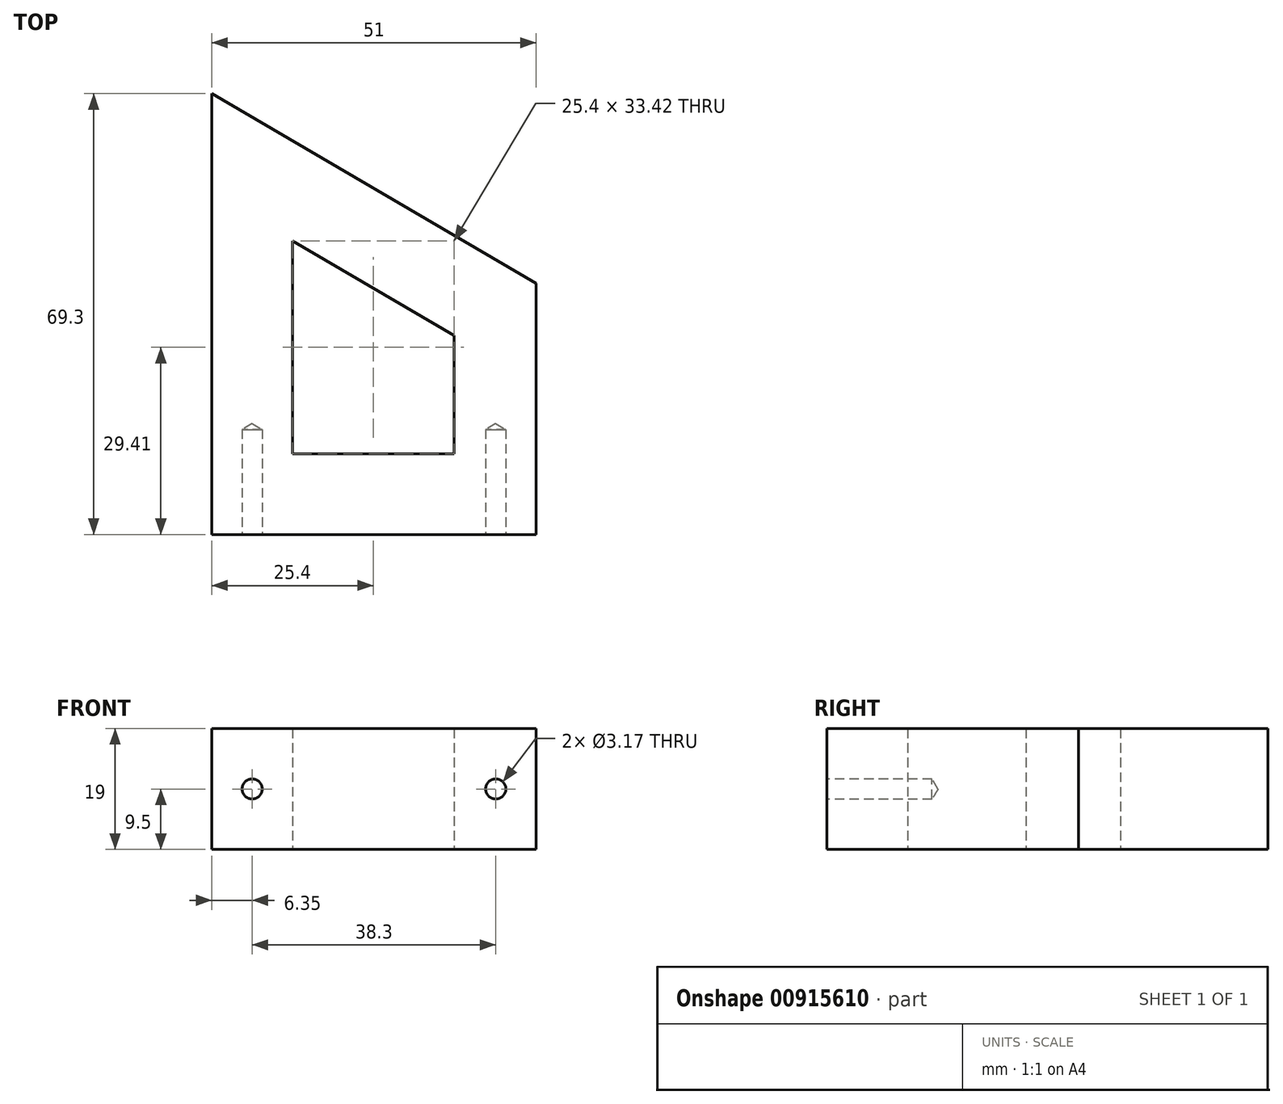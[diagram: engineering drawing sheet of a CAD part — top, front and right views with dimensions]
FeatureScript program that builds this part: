
annotation { "Feature Type Name" : "Feature", "Feature Type Description" : "" }
export const myFeature = defineFeature(function(context is Context, id is Id, definition is map)
    precondition{}
    {
        {
            var Q0;
            Q0=qCreatedBy(makeId("Top.planeOp"),FACE);
            var sketch = newSketch(context, id + "F0", { "sketchPlane" : qUnion([Q0])});
            skLineSegment(sketch, "E0", {"start": v(0, 0) * mm, "end": v(0, 69.3) * mm});
            skLineSegment(sketch, "E1", {"start": v(0, 0) * mm, "end": v(51, 0) * mm});
            skLineSegment(sketch, "E2", {"start": v(51, 0) * mm, "end": v(51, 39.5) * mm});
            skLineSegment(sketch, "E3", {"start": v(51, 39.5) * mm, "end": v(0, 69.3) * mm});
            skLineSegment(sketch, "E4", {"start": v(12.7, 12.7) * mm, "end": v(12.7, 46.12) * mm});
            skLineSegment(sketch, "E5", {"start": v(12.7, 46.12) * mm, "end": v(38.1, 31.28) * mm});
            skLineSegment(sketch, "E6", {"start": v(12.7, 12.7) * mm, "end": v(38.1, 12.7) * mm});
            skLineSegment(sketch, "E7", {"start": v(38.1, 12.7) * mm, "end": v(38.1, 31.28) * mm});
            skPoint(sketch, "E8.endSnap0", {"position": v(12.7, 29.41) * mm});
            skSolve(sketch);
        }
        {
            var Q0;
            Q0=makeQuery(id+"F0.imprint","IMPRINT",FACE,{"disambiguationData":[TD([[makeQuery(id+"F0.imprint","IMPRINT",EDGE,{"derivedFrom":sQuery(id+"F0.wireOp",EDGE,"E0")}),-1.0]])]});
            extrude(context, id + "F1", {"entities" : qUnion([Q0]), "depth" : 19 * mm, "offsetDistance" : 25.4 * mm});
        }
        {
            var Q0;
            Q0=makeQuery(id+"F1.opExtrude","SWEPT_FACE",FACE,{"disambiguationData":[OSD([sQuery(id+"F0.wireOp",EDGE,"E1")])]});
            var sketch = newSketch(context, id + "F2", { "sketchPlane" : qUnion([Q0])});
            skLineSegment(sketch, "E9", {"start": v(0, 9.5) * mm, "end": v(51, 9.5) * mm, "construction": true});
            skCircle(sketch, "E10", {"center": v(6.35, 9.5) * mm, "radius": 1.08 * mm});
            skCircle(sketch, "E11", {"center": v(44.65, 9.5) * mm, "radius": 1.08 * mm});
            skSolve(sketch);
        }
        {
            var Q0;
            Q0 = qSketchRegion(id + "F2", true);
            extrude(context, id + "F3", {"entities" : qUnion([Q0]), "operationType" : NewBodyOperationType.ADD, "oppositeDirection" : true, "depth" : 19.05 * mm, "hasOffset" : true, "offsetDistance" : 25.4 * mm});
        }
        {
            var Q0;
            Q0=makeQuery(id+"F1.opExtrude","SWEPT_FACE",FACE,{"disambiguationData":[OSD([sQuery(id+"F0.wireOp",EDGE,"E1")])]});
            var sketch = newSketch(context, id + "F4", { "sketchPlane" : qUnion([Q0])});
            skLineSegment(sketch, "E12", {"start": v(51, 9.5) * mm, "end": v(0, 9.5) * mm, "construction": true});
            skLineSegment(sketch, "E13", {"start": v(25.5, 19) * mm, "end": v(25.5, 0) * mm, "construction": true});
            skPoint(sketch, "E14", {"position": v(6.35, 9.5) * mm});
            skPoint(sketch, "E15.MirrorP", {"position": v(44.65, 9.5) * mm});
            skSolve(sketch);
        }
        {
            var Q0;
            Q0=sQuery(id+"F4.wireOp",VERTEX,"E14");
            var Q1;
            Q1=sQuery(id+"F4.wireOp",VERTEX,"E15.MirrorP");
            var Q2;
            Q2=makeQuery(id+"F1.opExtrude","SWEPT_BODY",BODY,{"disambiguationData":[OSD([sQuery(id+"F0.wireOp",EDGE,"E0"),sQuery(id+"F0.wireOp",EDGE,"E1"),sQuery(id+"F0.wireOp",EDGE,"E2"),sQuery(id+"F0.wireOp",EDGE,"E3"),sQuery(id+"F0.wireOp",EDGE,"E4"),sQuery(id+"F0.wireOp",EDGE,"E5"),sQuery(id+"F0.wireOp",EDGE,"E6"),sQuery(id+"F0.wireOp",EDGE,"E7")])]});
            hole(context, id + "F5", {"style" : HoleStyle.SIMPLE, "endStyle" : HoleEndStyle.BLIND, "holeDiameter" : 3.17 * mm, "majorDiameter" : 6.35 * mm, "holeDepth" : 16.5 * mm, "isTappedThrough" : true, "tappedDepth" : 12.7 * mm, "tapClearance" : 3, "locations" : qUnion([Q0, Q1]), "scope" : qUnion([Q2])});
        }
    });
